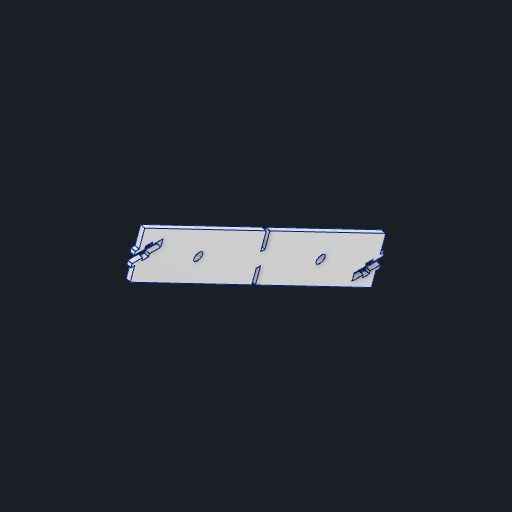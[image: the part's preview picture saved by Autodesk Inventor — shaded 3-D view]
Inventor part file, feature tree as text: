
AUTODESK INVENTOR PART (.ipt)
format: ipt  version: 2023 (Build 270158000, 158)  size: 200,192 bytes
history: native  units: in
note: dims shown in document units (in); Inventor stores cm internally (conversion verified against a paired STEP export)
features: reference x9, other x8, sketch x3, extrude x2, plane x1, hole x1
ambient origin geometry x8: Origin, YZ Plane, XZ Plane, XY Plane, X Axis, Y Axis, Z Axis, Center Point
bodies: Solid1 (feature_tree)
feature tree (24):
  plane  "Work Plane1"
  extrude  "Extrusion1"  Depth=0.5in
  hole  "Hole1"  [1 undecoded]
  extrude  "Extrusion2"  Depth=0.5in
  sketch  "Sketch1"  dims[d0=0.5in d1=0.5in]
  reference  "Reference1"
  reference  "Reference8"
  reference  "Reference9"
  reference  "Reference10"
  reference  "Reference11"
  reference  "Reference12"
  reference  "Reference13"
  sketch  "Sketch2"  dims[d2=0.5in d3=0.5in]
  sketch  "Sketch3"  dims[d4=0.5in d5=0.5in d6=0.125in d7=0.0in d9=0.266in d10=0.75in d11=0.507in d12=0.25in d13=0.5635in d14=0.536in d15=0.0in d16=0.85in d19=0.4375in d20=0.2in d21=0.85in d22=0.25in d23=0.25in d24=0.2in d25=0.4375in d26=0.0in d27=0.0in d28=0.015in d29=0.015in]
  reference  "Reference15"
  reference  "Reference16"
  other  "<userpath>\Desktop\WaccaController\Wacca Controller\Touch Segment\Touch Segment.iam"
  other  "Touch Segment.iam"
  other  "Touch Fifth:1"
  other  "Back Plate:1"
  other  "Center Plate:1"
  other  "Front Plate:1"
  other  "<userpath>\Desktop\Wacca Controller V3\Touch Segment\Touch Segment.iam"
  other  "Touch Fifth:5"
note: 1 required parameter value undecoded (feature->parameter linkage not recoverable at this tier; creation-order binding heuristic only, values carry confidence <= 0.55)
